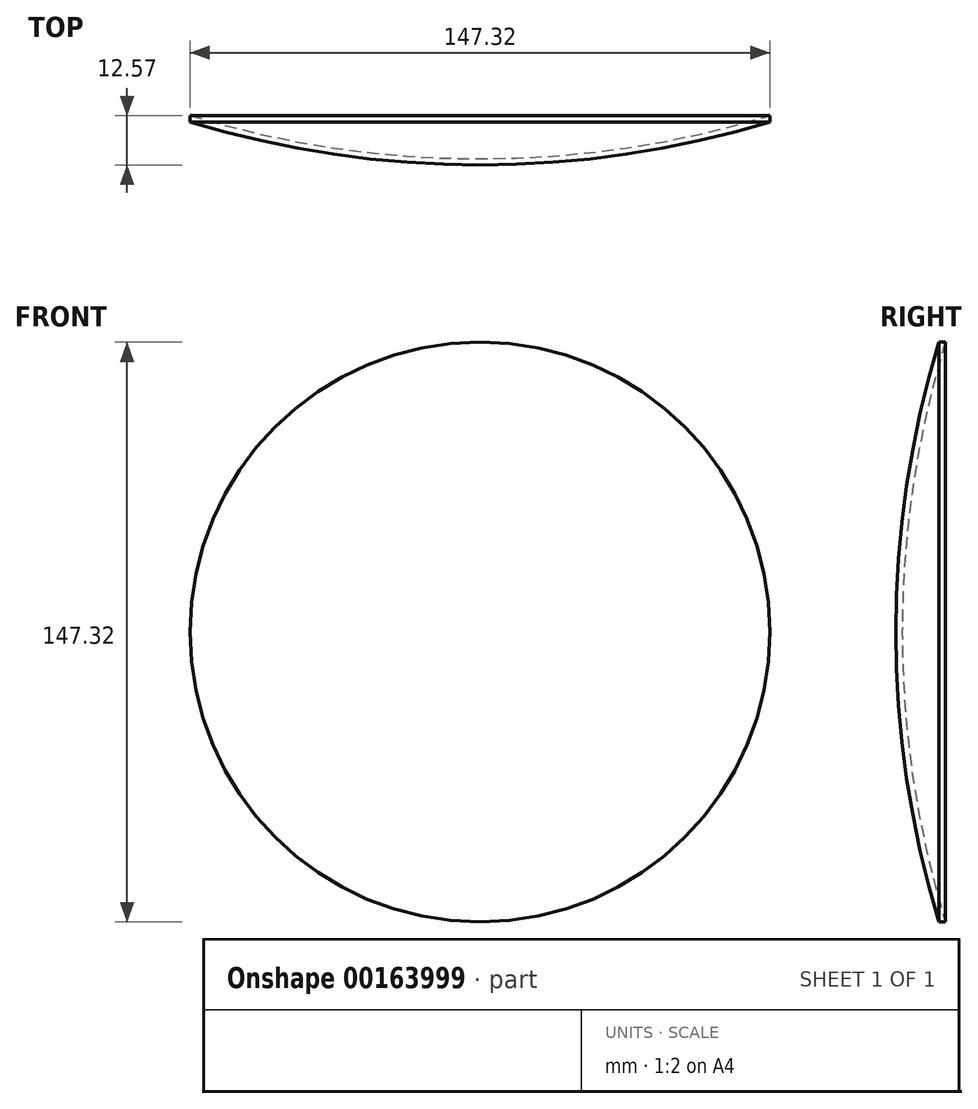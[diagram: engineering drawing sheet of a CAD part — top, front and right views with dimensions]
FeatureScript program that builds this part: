
annotation { "Feature Type Name" : "Feature", "Feature Type Description" : "" }
export const myFeature = defineFeature(function(context is Context, id is Id, definition is map)
    precondition{}
    {
        {
            var Q0;
            Q0=qCreatedBy(makeId("Front.planeOp"),FACE);
            var sketch = newSketch(context, id + "F0", { "sketchPlane" : qUnion([Q0])});
            skArc(sketch, "E0", {"start": v(0, -254) * mm, "mid": v(254, 0) * mm, "end": v(0, 254) * mm});
            skLineSegment(sketch, "E1", {"start": v(0, -254) * mm, "end": v(0, 254) * mm});
            skSolve(sketch);
        }
        {
            var Q0;
            Q0=makeQuery(id+"F0.imprint","IMPRINT",FACE,{"disambiguationData":[TD([[makeQuery(id+"F0.imprint","IMPRINT",EDGE,{"derivedFrom":sQuery(id+"F0.wireOp",EDGE,"E0")}),1.0]])]});
            var Q1;
            Q1=sQuery(id+"F0.wireOp",EDGE,"E1");
            revolve(context, id + "F1", {"entities" : qUnion([Q0]), "axis" : qUnion([Q1]), "revolveType" : RevolveType.FULL});
        }
        {
            var Q0;
            Q0=qCreatedBy(makeId("Front.planeOp"),FACE);
            var sketch = newSketch(context, id + "F2", { "sketchPlane" : qUnion([Q0])});
            skCircle(sketch, "E2", {"center": v(0, 0) * mm, "radius": 73.66 * mm});
            skSolve(sketch);
        }
        {
            var Q0;
            Q0 = qSketchRegion(id + "F2", true);
            extrude(context, id + "F3", {"entities" : qUnion([Q0]), "operationType" : NewBodyOperationType.INTERSECT, "depth" : 358.14 * mm});
        }
        {
            var Q0;
            Q0=qCreatedBy(makeId("Top.planeOp"),FACE);
            var sketch = newSketch(context, id + "F4", { "sketchPlane" : qUnion([Q0])});
            skArc(sketch, "E3", {"start": v(-252.41, 0) * mm, "mid": v(0, -252.41) * mm, "end": v(252.41, 0) * mm});
            skLineSegment(sketch, "E4", {"start": v(252.41, 0) * mm, "end": v(-252.41, 0) * mm});
            skSolve(sketch);
        }
        {
            var Q0;
            Q0=makeQuery(id+"F4.imprint","IMPRINT",FACE,{"disambiguationData":[TD([[makeQuery(id+"F4.imprint","IMPRINT",EDGE,{"derivedFrom":sQuery(id+"F4.wireOp",EDGE,"E3")}),1.0]])]});
            var Q1;
            Q1=sQuery(id+"F4.wireOp",EDGE,"E4");
            revolve(context, id + "F5", {"operationType" : NewBodyOperationType.REMOVE, "entities" : qUnion([Q0]), "axis" : qUnion([Q1]), "revolveType" : RevolveType.FULL, "oppositeDirection" : true});
        }
    });
